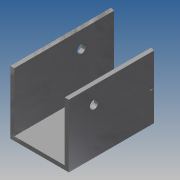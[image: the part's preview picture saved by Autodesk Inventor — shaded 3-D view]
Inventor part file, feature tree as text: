
AUTODESK INVENTOR PART (.ipt)
format: ipt  version: 2014 SP1 (Build 180222100, 222)  size: 115,712 bytes
history: native  units: in
note: dims shown in document units (in); Inventor stores cm internally (conversion verified against a paired STEP export)
features: sketch x5, other x3, plane x1
ambient origin geometry x8: Origin, YZ Plane, XZ Plane, XY Plane, X Axis, Y Axis, Z Axis, Center Point
bodies: Solid1 (feature_tree)
feature tree (9):
  other  "endChannel.ipt"
  other  "Solid1::endChannel.ipt"
  other  "TaggingFeature1"
  sketch  "Sketch1"  dims[d0=0.3937in]
  sketch  "Sketch2"  dims[d1=1.75in d2=1.75in d3=0.12in d4=3.0in d5=0.0in d6=2.0in d7=15.0deg d8=4.0in d9=0.0in d10=0.75in d11=0.5in d12=0.25in d17=1.0in d18=0.8108in d19=2.0in d20=0.5in d21=0.25in d26=1.0in d27=0.8108in d28=90.0deg d29=0.1in d30=0.1in d31=4.0in d32=0.0in]
  sketch  "Sketch3"
  sketch  "Sketch5"
  sketch  "Sketch6"
  plane  "Work Plane1"
